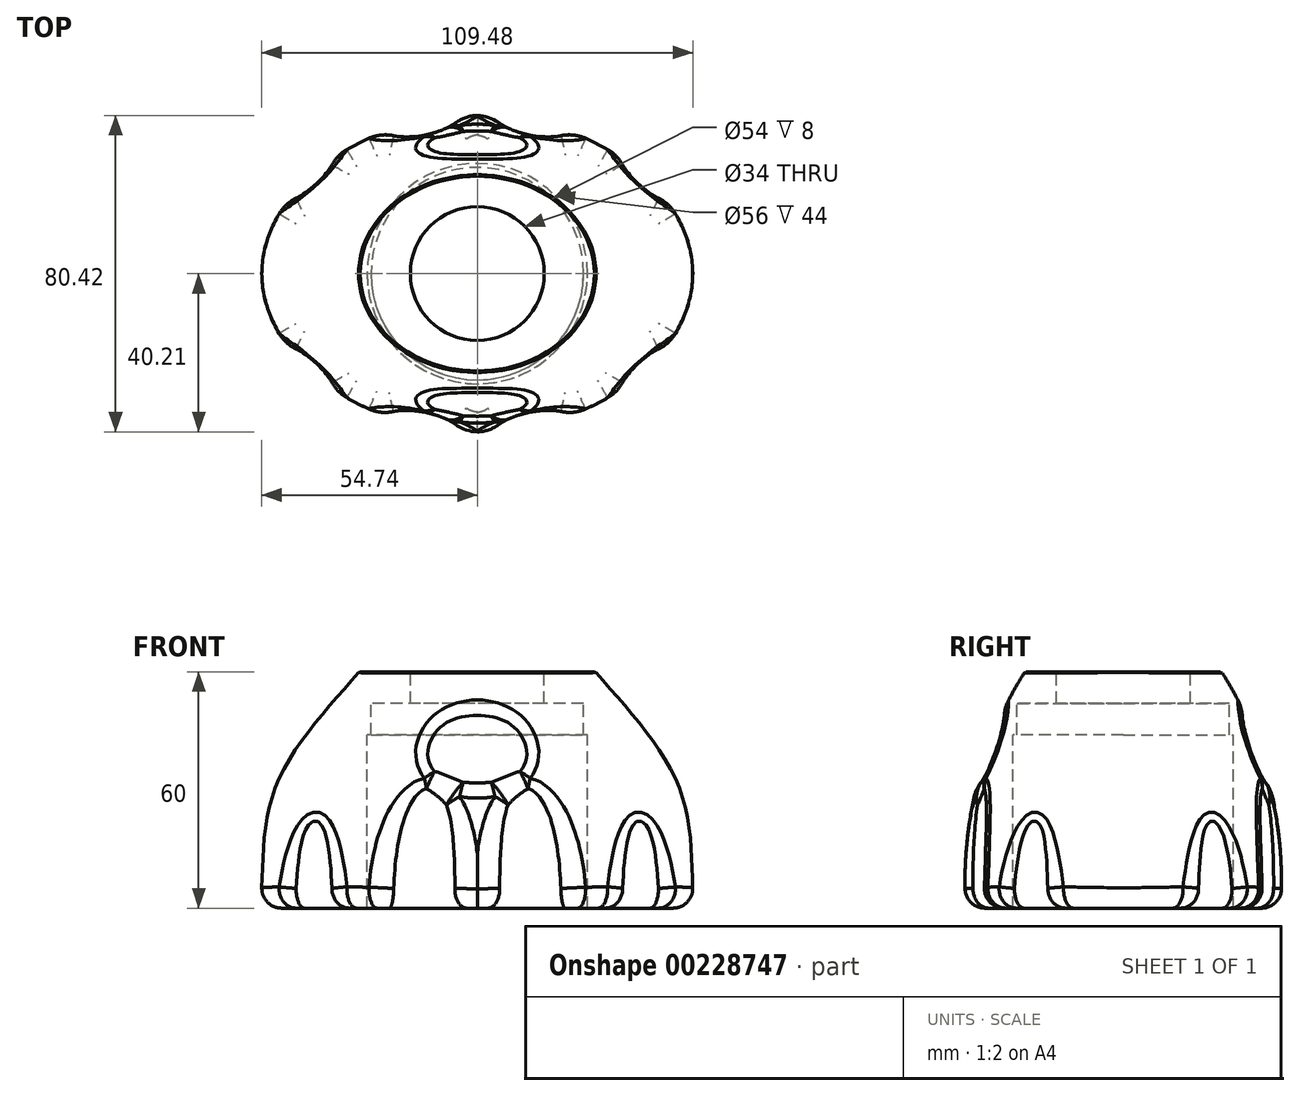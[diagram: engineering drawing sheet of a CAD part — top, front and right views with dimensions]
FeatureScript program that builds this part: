
annotation { "Feature Type Name" : "Feature", "Feature Type Description" : "" }
export const myFeature = defineFeature(function(context is Context, id is Id, definition is map)
    precondition{}
    {
        {
            var Q0;
            Q0=qCreatedBy(makeId("Top.planeOp"),FACE);
            var sketch = newSketch(context, id + "F0", { "sketchPlane" : qUnion([Q0])});
            skEllipticalArc(sketch, "E0", {});
            skLineSegment(sketch, "E1", {"start": v(0, -40) * mm, "end": v(0, 0) * mm});
            skLineSegment(sketch, "E2", {"start": v(0, 0) * mm, "end": v(-55, 0) * mm});
            skPoint(sketch, "E3.orphan", {"position": v(0, 40) * mm});
            const initialGuessF0  = {"E0": [0, 0, 1, 0, 0.055, 0.04, 3.141592653589793, 4.71238898038469]};
            skSetInitialGuess(sketch, initialGuessF0);
            skSolve(sketch);
        }
        {
            var Q0;
            Q0=qCreatedBy(makeId("Top.planeOp"),FACE);
            cPlane(context, id + "F1", {"entities" : qUnion([Q0]), "cplaneType" : CPlaneType.OFFSET, "offset" : 60 * mm, "width" : 150 * mm, "height" : 150 * mm});
        }
        {
            var Q0;
            Q0=qCreatedBy(id+"F1.planeOp",FACE);
            var sketch = newSketch(context, id + "F2", { "sketchPlane" : qUnion([Q0])});
            skEllipticalArc(sketch, "E4", {});
            skLineSegment(sketch, "E5", {"start": v(0, -25) * mm, "end": v(0, 0) * mm});
            skLineSegment(sketch, "E6", {"start": v(0, 0) * mm, "end": v(-30, 0) * mm});
            skPoint(sketch, "E7.orphan", {"position": v(0, 25) * mm});
            const initialGuessF2  = {"E4": [0, 0, 1, 0, 0.03, 0.025, 3.141592653589793, 4.71238898038469]};
            skSetInitialGuess(sketch, initialGuessF2);
            skSolve(sketch);
        }
        {
            var Q0;
            Q0=qCreatedBy(makeId("Front.planeOp"),FACE);
            var sketch = newSketch(context, id + "F3", { "sketchPlane" : qUnion([Q0])});
            skFitSpline(sketch, "E8", {"points": [v(-55, 0) * mm, v(-51.39, 30.37) * mm, v(-30, 60) * mm], "startDerivative": vector(4.54, 61.89) * mm, "endDerivative": vector(43.83, 50.5) * mm});
            skLineSegment(sketch, "E9", {"start": v(0, 0) * mm, "end": v(0, 59.88) * mm});
            skLineSegment(sketch, "E10", {"start": v(0, 59.88) * mm, "end": v(-30, 60) * mm});
            skLineSegment(sketch, "E11", {"start": v(-55, 0) * mm, "end": v(0, 0) * mm});
            skSolve(sketch);
        }
        {
            var Q0;
            Q0=qCreatedBy(makeId("Right.planeOp"),FACE);
            var sketch = newSketch(context, id + "F4", { "sketchPlane" : qUnion([Q0])});
            skFitSpline(sketch, "E12", {"points": [v(-40, 0) * mm, v(-36.94, 32.38) * mm, v(-25, 60) * mm], "startDerivative": vector(-4.29, 65.18) * mm, "endDerivative": vector(34.4, 54.17) * mm});
            skSolve(sketch);
        }
        {
            var Q0;
            Q0=makeQuery(id+"F0.imprint","IMPRINT",FACE,{"disambiguationData":[TD([[makeQuery(id+"F0.imprint","IMPRINT",EDGE,{"derivedFrom":sQuery(id+"F0.wireOp",EDGE,"E0")}),1.0]])]});
            var Q1;
            Q1=makeQuery(id+"F2.imprint","IMPRINT",FACE,{"disambiguationData":[TD([[makeQuery(id+"F2.imprint","IMPRINT",EDGE,{"derivedFrom":sQuery(id+"F2.wireOp",EDGE,"E4")}),1.0]])]});
            var Q2;
            Q2=sQuery(id+"F3.wireOp",EDGE,"E8");
            var Q3;
            Q3=sQuery(id+"F4.wireOp",EDGE,"E12");
            loft(context, id + "F5", {"addGuides" : true, "sheetProfilesArray" : [{ "sheetProfileEntities" : qUnion([Q0]) }, { "sheetProfileEntities" : qUnion([Q1]) }], "guidesArray" : [{ "guideEntities" : qUnion([Q2]), "guideDerivativeType" : LoftGuideDerivativeType.DEFAULT, "guideDerivativeMagnitude" : 1 }, { "guideEntities" : qUnion([Q3]), "guideDerivativeType" : LoftGuideDerivativeType.DEFAULT, "guideDerivativeMagnitude" : 1 }]});
        }
        {
            var Q0;
            Q0=qCreatedBy(id+"F1.planeOp",FACE);
            var sketch = newSketch(context, id + "F6", { "sketchPlane" : qUnion([Q0])});
            skLineSegment(sketch, "E13", {"start": v(0, 0) * mm, "end": v(-19.53, -53.66) * mm, "construction": true});
            skLineSegment(sketch, "E14", {"start": v(0, 0) * mm, "end": v(-60.43, -34.9) * mm, "construction": true});
            skLineSegment(sketch, "E15", {"start": v(-43.08, -24.87) * mm, "end": v(-11.59, 9.5) * mm, "construction": true});
            skLineSegment(sketch, "E16", {"start": v(-14.07, -38.67) * mm, "end": v(-9.87, -16.82) * mm, "construction": true});
            skLineSegment(sketch, "E17", {"start": v(-14.07, -38.67) * mm, "end": v(-4.25, -40.56) * mm, "construction": true});
            skLineSegment(sketch, "E18", {"start": v(-43.08, -24.87) * mm, "end": v(-36.44, -30.95) * mm, "construction": true});
            skEllipse(sketch, "E19", {"center": v(-43.08, -24.87) * mm, "majorRadius": 9 * mm, "minorRadius": 3 * mm, "majorAxis": v(0.74, -0.68)});
            skEllipse(sketch, "E20", {"center": v(-14.07, -38.67) * mm, "majorRadius": 10 * mm, "minorRadius": 3.5 * mm, "majorAxis": v(0.98, -0.19)});
            skSolve(sketch);
        }
        {
            var Q0;
            Q0 = qSketchRegion(id + "F6", true);
            extrude(context, id + "F7", {"entities" : qUnion([Q0]), "operationType" : NewBodyOperationType.REMOVE, "endBound" : BoundingType.THROUGH_ALL, "oppositeDirection" : true, "depth" : 25 * mm});
        }
        {
            var Q0;
            Q0=makeQuery(id+"F7.boolean.opBoolean","INTERSECT",EDGE,{"derivedFrom":[makeQuery(id+"F5.opLoft","SWEPT_FACE",FACE,{"disambiguationData":[OSD([sQuery(id+"F0.wireOp",EDGE,"E0"),sQuery(id+"F0.wireOp",EDGE,"E1"),sQuery(id+"F0.wireOp",EDGE,"E2"),sQuery(id+"F2.wireOp",EDGE,"E4"),sQuery(id+"F2.wireOp",EDGE,"E5"),sQuery(id+"F2.wireOp",EDGE,"E6"),sQuery(id+"F3.wireOp",EDGE,"E8"),sQuery(id+"F4.wireOp",EDGE,"E12")])]}),makeQuery(id+"F7.opExtrude","SWEPT_FACE",FACE,{"disambiguationData":[OSD([sQuery(id+"F6.wireOp",EDGE,"E19")])]})]});
            var Q1;
            Q1=makeQuery(id+"F7.boolean.opBoolean","INTERSECT",EDGE,{"derivedFrom":[makeQuery(id+"F5.opLoft","SWEPT_FACE",FACE,{"disambiguationData":[OSD([sQuery(id+"F0.wireOp",EDGE,"E0"),sQuery(id+"F0.wireOp",EDGE,"E1"),sQuery(id+"F0.wireOp",EDGE,"E2"),sQuery(id+"F2.wireOp",EDGE,"E4"),sQuery(id+"F2.wireOp",EDGE,"E5"),sQuery(id+"F2.wireOp",EDGE,"E6"),sQuery(id+"F3.wireOp",EDGE,"E8"),sQuery(id+"F4.wireOp",EDGE,"E12")])]}),makeQuery(id+"F7.opExtrude","SWEPT_FACE",FACE,{"disambiguationData":[OSD([sQuery(id+"F6.wireOp",EDGE,"E20")])]})]});
            fillet(context, id + "F8", {"entities" : qUnion([Q0, Q1]), "radius" : 10 * mm, "tangentPropagation" : true, "allowEdgeOverflow" : false});
        }
        {
            var Q0;
            Q0=makeQuery(id+"F5.opLoft","CAP_FACE",FACE,{"disambiguationData":[OSD([makeQuery(id+"F2.imprint","IMPRINT",FACE,{"disambiguationData":[TD([[makeQuery(id+"F2.imprint","IMPRINT",EDGE,{"derivedFrom":sQuery(id+"F2.wireOp",EDGE,"E4")}),1.0]])]})])],"isStart":true});
            var sketch = newSketch(context, id + "F9", { "sketchPlane" : qUnion([Q0])});
            skArc(sketch, "E21", {"start": v(-17, 0) * mm, "mid": v(-8.18, -14.9) * mm, "end": v(9.13, -14.34) * mm});
            skLineSegment(sketch, "E22", {"start": v(0, 0) * mm, "end": v(-17, 0) * mm});
            skLineSegment(sketch, "E23", {"start": v(0, -17) * mm, "end": v(0, 0) * mm});
            skSolve(sketch);
        }
        {
            var Q0;
            Q0 = qSketchRegion(id + "F9", true);
            extrude(context, id + "F10", {"entities" : qUnion([Q0]), "operationType" : NewBodyOperationType.REMOVE, "oppositeDirection" : true, "depth" : 8 * mm});
        }
        {
            var Q0;
            Q0=makeQuery(id+"F10.boolean.opBoolean","COPY",FACE,{"derivedFrom":makeQuery(id+"F10.opExtrude","CAP_FACE",FACE,{"disambiguationData":[OSD([sQuery(id+"F9.wireOp",EDGE,"E21"),sQuery(id+"F9.wireOp",EDGE,"E22"),sQuery(id+"F9.wireOp",EDGE,"E23")])],"isStart":false})});
            var sketch = newSketch(context, id + "F11", { "sketchPlane" : qUnion([Q0])});
            skCircle(sketch, "E24", {"center": v(0, 0) * mm, "radius": 27 * mm});
            skSolve(sketch);
        }
        {
            var Q0;
            Q0=qSketchRegion(id+"F11",true);
            extrude(context, id + "F12", {"entities" : qUnion([Q0]), "operationType" : NewBodyOperationType.REMOVE, "endBound" : BoundingType.THROUGH_ALL, "oppositeDirection" : true, "depth" : 50 * mm});
        }
        {
            var Q0;
            Q0=makeQuery(id+"F12.boolean.opBoolean","COPY",FACE,{"derivedFrom":makeQuery(id+"F12.opExtrude","CAP_FACE",FACE,{"disambiguationData":[OSD([sQuery(id+"F11.wireOp",EDGE,"E24")])],"isStart":true})});
            cPlane(context, id + "F13", {"entities" : qUnion([Q0]), "cplaneType" : CPlaneType.OFFSET, "offset" : 8 * mm, "width" : 150 * mm, "height" : 150 * mm});
        }
        {
            var Q0;
            Q0=qCreatedBy(id+"F13.planeOp",FACE);
            var sketch = newSketch(context, id + "F14", { "sketchPlane" : qUnion([Q0])});
            skCircle(sketch, "E25", {"center": v(0, 0) * mm, "radius": 28 * mm});
            skSolve(sketch);
        }
        {
            var Q0;
            Q0=qSketchRegion(id+"F14",true);
            extrude(context, id + "F15", {"entities" : qUnion([Q0]), "operationType" : NewBodyOperationType.REMOVE, "endBound" : BoundingType.THROUGH_ALL, "depth" : 15 * mm});
        }
        {
            var Q0;
            Q0=qCreatedBy(id+"F13.planeOp",FACE);
            cPlane(context, id + "F16", {"entities" : qUnion([Q0]), "cplaneType" : CPlaneType.OFFSET, "offset" : 28 * mm, "width" : 150 * mm, "height" : 150 * mm});
        }
        {
            var Q0;
            Q0=qCreatedBy(id+"F16.planeOp",FACE);
            var sketch = newSketch(context, id + "F17", { "sketchPlane" : qUnion([Q0])});
            skCircle(sketch, "E26", {"center": v(0, 0) * mm, "radius": 28.5 * mm});
            skSolve(sketch);
        }
        {
            var Q0;
            {var subQ0=sQuery(id+"FLK4nbVgcjfgiuH_1.wireOp",EDGE,"mpRuSKhc-iqaz-u3ej-QRg1-r9homqWtoDlk");var subQ1=sQuery(id+"FLK4nbVgcjfgiuH_1.wireOp",EDGE,"dBLUuZUS-x4L3-xRmu-ywpQ-NXTnD1bctG09");var subQ2=sQuery(id+"FLK4nbVgcjfgiuH_1.wireOp",EDGE,"JFAcJmmm-pDXh-Up5B-Dt13-QZXfunTNarxs");var subQ3=sQuery(id+"F2.wireOp",EDGE,"E5");var subQ4=sQuery(id+"F2.wireOp",EDGE,"E6");var subQ5=sQuery(id+"F2.wireOp",EDGE,"E4");Q0=makeQuery(id+"FatG9CThDeujZQO_1.boolean.opBoolean","MERGE",FACE,{"derivedFrom":[makeQuery(id+"F5.opLoft","SWEPT_FACE",FACE,{"disambiguationData":[OSD([sQuery(id+"F0.wireOp",EDGE,"E1"),sQuery(id+"F0.wireOp",EDGE,"E2"),subQ3,subQ4,sQuery(id+"F4.wireOp",EDGE,"E12")])]}),makeQuery(id+"FatG9CThDeujZQO_1.opLoft","SWEPT_FACE",FACE,{"disambiguationData":[OSD([subQ5,subQ3,subQ4,subQ2,subQ1,subQ0]),TDD([makeQuery(id+"F2.imprint","INTERSECT",VERTEX,{"derivedFrom":[subQ5,subQ3]}),makeQuery(id+"F2.imprint","INTERSECT",VERTEX,{"derivedFrom":[subQ3,subQ4]}),makeQuery(id+"F2.imprint","IMPRINT",EDGE,{"derivedFrom":subQ3}),makeQuery(id+"FLK4nbVgcjfgiuH_1.imprint","INTERSECT",VERTEX,{"derivedFrom":[subQ2,subQ0]}),makeQuery(id+"FLK4nbVgcjfgiuH_1.imprint","INTERSECT",VERTEX,{"derivedFrom":[subQ1,subQ0]}),makeQuery(id+"FLK4nbVgcjfgiuH_1.imprint","IMPRINT",EDGE,{"derivedFrom":subQ0})])]})]});}
            var sketch = newSketch(context, id + "F18", { "sketchPlane" : qUnion([Q0])});
            skLineSegment(sketch, "E27", {"start": v(-66.77, 41) * mm, "end": v(63.6, 41) * mm, "construction": true});
            skEllipse(sketch, "E28", {"center": v(-34.32, 41) * mm, "majorRadius": 11 * mm, "minorRadius": 2.17 * mm, "majorAxis": v(0.32, 0.95)});
            skSolve(sketch);
        }
        {
            var Q0;
            Q0 = qSketchRegion(id + "F18", true);
            extrude(context, id + "F19", {"entities" : qUnion([Q0]), "operationType" : NewBodyOperationType.REMOVE, "oppositeDirection" : true, "depth" : 25 * mm});
        }
        {
            var Q0;
            Q0=makeQuery(id+"F19.boolean.opBoolean","INTERSECT",EDGE,{"derivedFrom":[makeQuery(id+"F5.opLoft","SWEPT_FACE",FACE,{"disambiguationData":[OSD([sQuery(id+"F0.wireOp",EDGE,"E0"),sQuery(id+"F0.wireOp",EDGE,"E1"),sQuery(id+"F0.wireOp",EDGE,"E2"),sQuery(id+"F2.wireOp",EDGE,"E4"),sQuery(id+"F2.wireOp",EDGE,"E5"),sQuery(id+"F2.wireOp",EDGE,"E6"),sQuery(id+"F3.wireOp",EDGE,"E8"),sQuery(id+"F4.wireOp",EDGE,"E12")])]}),makeQuery(id+"F19.opExtrude","SWEPT_FACE",FACE,{"disambiguationData":[OSD([sQuery(id+"F18.wireOp",EDGE,"E28")])]})]});
            fillet(context, id + "F20", {"entities" : qUnion([Q0]), "radius" : 10 * mm, "tangentPropagation" : true, "allowEdgeOverflow" : false});
        }
        {
            var Q0;
            Q0=makeQuery(id+"F7.boolean.opBoolean","INTERSECT",EDGE,{"derivedFrom":[makeQuery(id+"F5.opLoft","CAP_FACE",FACE,{"disambiguationData":[OSD([makeQuery(id+"F0.imprint","IMPRINT",FACE,{"disambiguationData":[TD([[makeQuery(id+"F0.imprint","IMPRINT",EDGE,{"derivedFrom":sQuery(id+"F0.wireOp",EDGE,"E0")}),1.0]])]})])],"isStart":true}),makeQuery(id+"F7.opExtrude","SWEPT_FACE",FACE,{"disambiguationData":[OSD([sQuery(id+"F6.wireOp",EDGE,"E20")])]})]});
            fillet(context, id + "F21", {"entities" : qUnion([Q0]), "radius" : 5 * mm, "tangentPropagation" : true, "allowEdgeOverflow" : false});
        }
        {
            var Q0;
            Q0=makeQuery(id+"F5.opLoft","SWEPT_BODY",BODY,{"disambiguationData":[OSD([makeQuery(id+"F0.imprint","IMPRINT",FACE,{"disambiguationData":[TD([[makeQuery(id+"F0.imprint","IMPRINT",EDGE,{"derivedFrom":sQuery(id+"F0.wireOp",EDGE,"E0")}),1.0]])]}),makeQuery(id+"F2.imprint","IMPRINT",FACE,{"disambiguationData":[TD([[makeQuery(id+"F2.imprint","IMPRINT",EDGE,{"derivedFrom":sQuery(id+"F2.wireOp",EDGE,"E4")}),1.0]])]}),sQuery(id+"F3.wireOp",EDGE,"E8"),sQuery(id+"F4.wireOp",EDGE,"E12")])]});
            var Q1;
            Q1=qCreatedBy(makeId("Right.planeOp"),FACE);
            mirror(context, id + "F22", {"operationType" : NewBodyOperationType.ADD, "entities" : qUnion([Q0]), "mirrorPlane" : qUnion([Q1])});
        }
        {
            var Q0;
            Q0=makeQuery(id+"F5.opLoft","SWEPT_BODY",BODY,{"disambiguationData":[OSD([makeQuery(id+"F0.imprint","IMPRINT",FACE,{"disambiguationData":[TD([[makeQuery(id+"F0.imprint","IMPRINT",EDGE,{"derivedFrom":sQuery(id+"F0.wireOp",EDGE,"E0")}),1.0]])]}),makeQuery(id+"F2.imprint","IMPRINT",FACE,{"disambiguationData":[TD([[makeQuery(id+"F2.imprint","IMPRINT",EDGE,{"derivedFrom":sQuery(id+"F2.wireOp",EDGE,"E4")}),1.0]])]}),sQuery(id+"F3.wireOp",EDGE,"E8"),sQuery(id+"F4.wireOp",EDGE,"E12")])]});
            var Q1;
            Q1=qCreatedBy(makeId("Front.planeOp"),FACE);
            mirror(context, id + "F23", {"operationType" : NewBodyOperationType.ADD, "entities" : qUnion([Q0]), "mirrorPlane" : qUnion([Q1])});
        }
        {
            var Q0;
            Q0=makeQuery(id+"F5.opLoft","MID_CAP_EDGE",EDGE,{"disambiguationData":[OSD([sQuery(id+"F2.wireOp",EDGE,"E4"),sQuery(id+"F3.wireOp",EDGE,"E8"),sQuery(id+"F4.wireOp",EDGE,"E12")])],"capPos":1.0});
            chamfer(context, id + "F24", {"entities" : qUnion([Q0]), "width" : .5 * mm, "tangentPropagation" : true});
        }
    });
